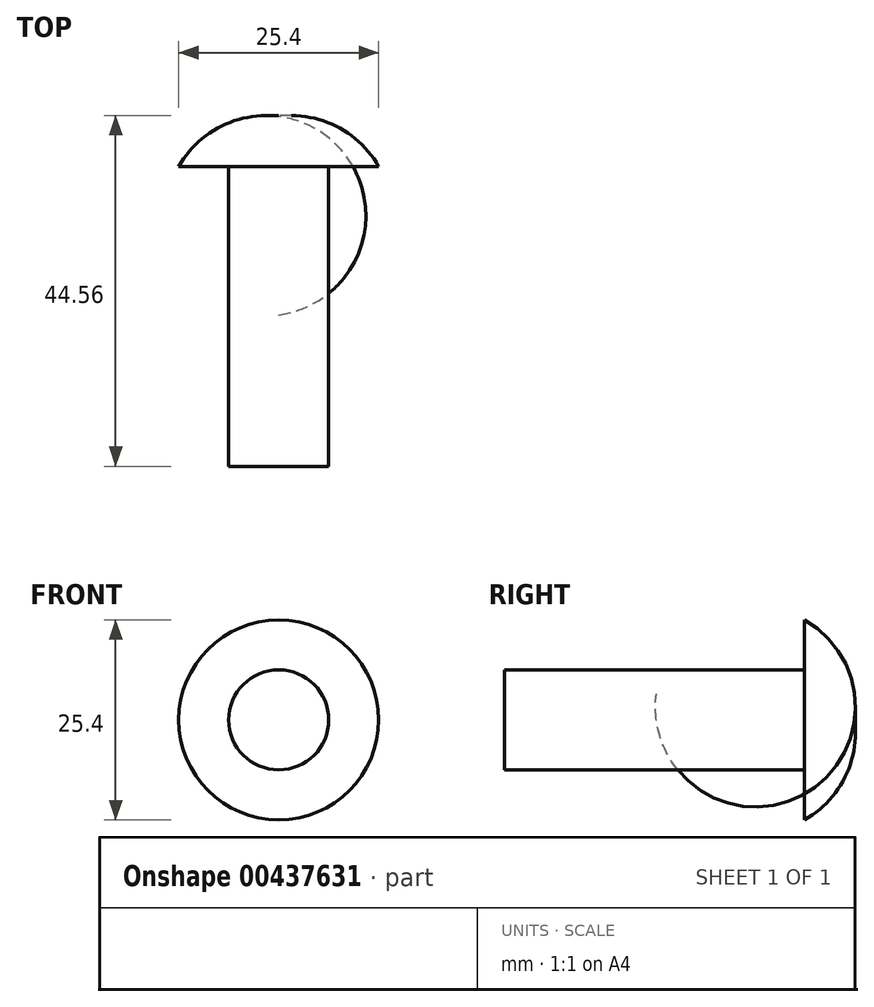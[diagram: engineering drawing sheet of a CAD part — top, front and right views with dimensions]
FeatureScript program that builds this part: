
annotation { "Feature Type Name" : "Feature", "Feature Type Description" : "" }
export const myFeature = defineFeature(function(context is Context, id is Id, definition is map)
    precondition{}
    {
        {
            var Q0;
            Q0=qCreatedBy(makeId("Front.planeOp"),FACE);
            var sketch = newSketch(context, id + "F0", { "sketchPlane" : qUnion([Q0])});
            skCircle(sketch, "E0", {"center": v(0, 0) * mm, "radius": 6.35 * mm});
            skSolve(sketch);
        }
        {
            var Q0;
            Q0=qSketchRegion(id+"F0",true);
            extrude(context, id + "F1", {"entities" : qUnion([Q0]), "depth" : 38.1 * mm, "offsetDistance" : 25.4 * mm});
        }
        {
            var Q0;
            Q0=qCreatedBy(makeId("Top.planeOp"),FACE);
            var sketch = newSketch(context, id + "F2", { "sketchPlane" : qUnion([Q0])});
            skLineSegment(sketch, "E1", {"start": v(0, 0) * mm, "end": v(12.7, 0) * mm});
            skArc(sketch, "E2", {"start": v(12.7, 0) * mm, "mid": v(7.32, 5.12) * mm, "end": v(0, 6.35) * mm});
            skLineSegment(sketch, "E3", {"start": v(0, 6.35) * mm, "end": v(0, 0) * mm});
            skSolve(sketch);
        }
        {
            var Q0;
            Q0=qSketchRegion(id+"F2",true);
            var Q1;
            Q1=sQuery(id+"F2.wireOp",EDGE,"E3");
            revolve(context, id + "F3", {"operationType" : NewBodyOperationType.ADD, "entities" : qUnion([Q0]), "axis" : qUnion([Q1]), "revolveType" : RevolveType.FULL});
        }
    });
